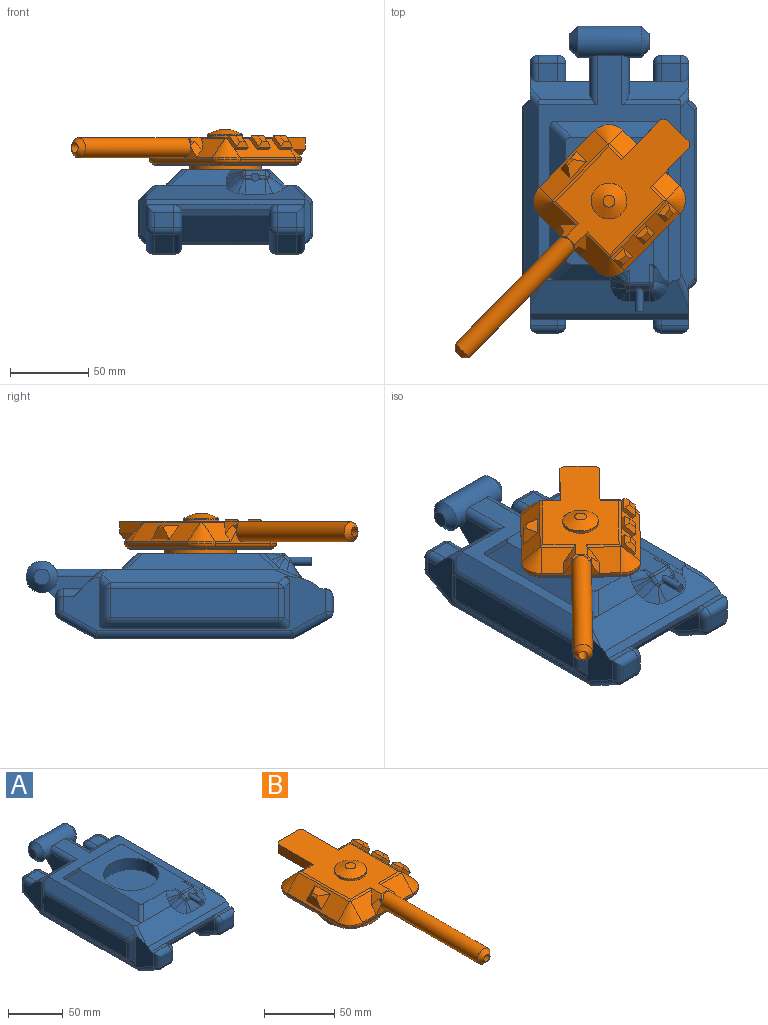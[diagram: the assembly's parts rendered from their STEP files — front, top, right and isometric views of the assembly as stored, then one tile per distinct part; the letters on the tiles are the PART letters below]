
ASSEMBLY  parts=2 mates=1
PART A: 179 faces, bbox 117.9x202.1x63.1 mm
  f0: plane 4.26x0.4mm, normal (0,-1,0), area 1.6mm2, adj f75,f86,f89,f96
  f1: plane 147.71x93.76mm, normal (0,0,1), area 3002mm2, adj f6,f44,f47,f48,f49,f51,f52,f54
  f2: plane 25.4x11.06mm, normal (0,0.71,-0.71), area 397.3mm2, adj f60,f61,f62,f63
  f3: plane 20.32x5.08mm, normal (0,1,0), area 83mm2, adj f4,f5,f60,f129
  f4: plane 55.88x20.32mm, normal (0,0.71,-0.71), area 1332.1mm2, adj f3,f9,f10,f23,f31,f60,f61,f62
  f5: plane 41.72x18.43mm, normal (0,0.71,0.71), area 577.8mm2, adj f3,f6,f13,f16,f60,f67,f74,f152
  f6: plane 39.72x5.32mm, normal (0,0.38,0.92), area 137.2mm2, adj f1,f5,f67,f74
  f7: plane 5.7x3.16mm, normal (0,-0.71,0.71), area 7.4mm2, adj f50,f51,f80,f99
  f8: plane 66.04x2.98mm, normal (0,-1,0), area 176.7mm2, adj f15,f46,f141,f165
  f9: plane 20.32x5.08mm, normal (0,1,0), area 83mm2, adj f4,f14,f61,f153
  f10: plane 109.66x55.88mm, normal (0,0,-1), area 6127.6mm2, adj f4,f23,f31,f45
  f11: plane 55.88x17.34mm, normal (0,-0.71,-0.71), area 1370.6mm2, adj f23,f31,f45,f46
  f12: plane 169.57x36.22mm, normal (-1,0,0), area 1238.2mm2, adj f14,f15,f30,f44,f48,f71,f73,f102
  f13: plane 169.57x36.22mm, normal (1,0,0), area 1238.2mm2, adj f5,f15,f18,f44,f47,f72,f74,f105
  f14: plane 41.72x18.43mm, normal (0,0.71,0.71), area 577.8mm2, adj f9,f12,f24,f49,f61,f66,f73,f176
  f15: plane 101.6x3.72mm, normal (0,-0.71,0.71), area 534.5mm2, adj f8,f12,f13,f18,f30,f44
  f16: plane 12.7x11.79mm, normal (0,0,1), area 149.7mm2, adj f5,f43,f129,f152
  f17: plane 12.7x9.7mm, normal (0,1,0), area 123.1mm2, adj f42,f43,f131,f150
  f18: plane 17.78x3.45mm, normal (0,0,1), area 61.4mm2, adj f13,f15,f38,f141
  f19: plane 12.7x9.7mm, normal (0,-1,0), area 123.1mm2, adj f38,f39,f139,f142
  f20: plane 21.63x12.7mm, normal (0,-0.48,-0.88), area 313.4mm2, adj f39,f40,f137,f144
  f21: plane 124.39x12.7mm, normal (0,0,-1), area 1579.8mm2, adj f40,f41,f135,f146
  f22: plane 21.63x12.7mm, normal (0,0.48,-0.88), area 313.4mm2, adj f41,f42,f133,f148
  f23: plane 167.64x21.59mm, normal (-1,0,0), area 680.5mm2, adj f4,f10,f11,f45,f46,f129,f131,f133
  f24: plane 12.7x11.79mm, normal (0,0,1), area 149.7mm2, adj f14,f37,f153,f176
  f25: plane 12.7x9.7mm, normal (0,1,0), area 123.1mm2, adj f36,f37,f155,f174
  f26: plane 21.63x12.7mm, normal (0,0.48,-0.88), area 313.4mm2, adj f35,f36,f157,f172
  f27: plane 124.39x12.7mm, normal (0,0,-1), area 1579.8mm2, adj f34,f35,f159,f170
  f28: plane 21.63x12.7mm, normal (0,-0.48,-0.88), area 313.4mm2, adj f33,f34,f161,f168
  f29: plane 12.7x9.7mm, normal (0,-1,0), area 123.1mm2, adj f32,f33,f163,f166
  f30: plane 17.78x3.45mm, normal (0,0,1), area 61.4mm2, adj f12,f15,f32,f165
  f31: plane 167.64x21.59mm, normal (1,0,0), area 680.5mm2, adj f4,f10,f11,f45,f46,f153,f155,f157
  f32: cylinder r=5.08mm len=17.78mm, axis (-1,0,0), area 121.6mm2, adj f29,f30,f164,f166
  f33: cylinder r=5.08mm len=12.7mm, axis (-1,0,0), area 68.9mm2, adj f28,f29,f162,f167
  f34: cylinder r=5.08mm len=12.7mm, axis (-1,0,0), area 32.4mm2, adj f27,f28,f160,f169
  f35: cylinder r=5.08mm len=12.7mm, axis (-1,0,0), area 32.4mm2, adj f26,f27,f158,f171
  f36: cylinder r=5.08mm len=12.7mm, axis (-1,0,0), area 68.9mm2, adj f25,f26,f156,f173
  f37: cylinder r=5.08mm len=12.7mm, axis (-1,0,0), area 101.3mm2, adj f24,f25,f154,f175
  f38: cylinder r=5.08mm len=17.78mm, axis (1,0,0), area 121.6mm2, adj f18,f19,f140,f142
  f39: cylinder r=5.08mm len=12.7mm, axis (1,0,0), area 68.9mm2, adj f19,f20,f138,f143
  f40: cylinder r=5.08mm len=12.7mm, axis (1,0,0), area 32.4mm2, adj f20,f21,f136,f145
  f41: cylinder r=5.08mm len=12.7mm, axis (1,0,0), area 32.4mm2, adj f21,f22,f134,f147
  f42: cylinder r=5.08mm len=12.7mm, axis (1,0,0), area 68.9mm2, adj f17,f22,f132,f149
  f43: cylinder r=5.08mm len=12.7mm, axis (1,0,0), area 101.3mm2, adj f16,f17,f130,f151
  f44: plane 101.62x21.7mm, normal (0,-0.38,0.92), area 1735.6mm2, adj f1,f12,f13,f15,f53,f71,f72,f93
  f45: plane 55.88x3.59mm, normal (0,-0.38,-0.92), area 217.3mm2, adj f10,f11,f23,f31
  f46: plane 56.81x3.61mm, normal (0,-0.92,-0.38), area 217.9mm2, adj f8,f11,f23,f31,f141,f165
  f47: plane 121.65x8.67mm, normal (0.71,0,0.71), area 1384.6mm2, adj f1,f13,f72,f74,f120,f122,f123
  f48: plane 121.65x8.67mm, normal (-0.71,0,0.71), area 1384.6mm2, adj f1,f12,f71,f73,f108,f113,f114
  f49: plane 39.72x5.32mm, normal (0,0.38,0.92), area 137.2mm2, adj f1,f14,f66,f73
  f50: plane 98.48x61.43mm, normal (0,0,1), area 2680.2mm2, adj f7,f51,f52,f53,f54,f55,f68,f69
  f51: plane 99.76x10.16mm, normal (0.71,0,0.71), area 1278.1mm2, adj f1,f7,f50,f68,f99
  f52: plane 69.02x10.16mm, normal (0,0.71,0.71), area 845.7mm2, adj f1,f50,f68,f69
  f53: plane 39.08x10.2mm, normal (0,-0.71,0.71), area 444.2mm2, adj f44,f50,f70,f90,f91,f92,f93
  f54: plane 94.42x10.16mm, normal (-0.71,0,0.71), area 1210.6mm2, adj f1,f50,f69,f70
  f55: cylinder r=25.4mm len=50.8mm, axis (0,0,1), area 2026.8mm2, adj f50,f56
  f56: plane 50.8x50.8mm, normal (0,0,1), area 2026.8mm2, adj f55
  f57: plane 4.26x0.4mm, normal (0,-1,0), area 1.6mm2, adj f75,f77,f78,f96
  f58: plane 12.25x3.44mm, normal (1,0,0), area 16mm2, adj f80,f81,f98,f99
  f59: plane 12.7x3.59mm, normal (0,-0.71,0.71), area 55.5mm2, adj f75,f78,f81,f84,f87,f89
  f60: plane 28.87x20.32mm, normal (1,0,0), area 389mm2, adj f2,f3,f4,f5,f62,f63,f67
  f61: plane 28.87x20.32mm, normal (-1,0,0), area 389mm2, adj f2,f4,f9,f14,f62,f63,f66
  f62: plane 25.4x17.81mm, normal (0,0,-1), area 452.5mm2, adj f2,f4,f60,f61
  f63: cylinder r=10.16mm len=40.64mm, axis (1,0,0), area 2190.3mm2, adj f1,f2,f60,f61,f66,f67,f177,f178
  f64: plane 10.16x10.16mm, normal (-1,0,0), area 81.1mm2, adj f178
  f65: plane 10.16x10.16mm, normal (1,0,0), area 81.1mm2, adj f177
  f66: cylinder r=5.08mm len=31.44mm, axis (0,-1,0), area 216.8mm2, adj f1,f14,f49,f61,f63
  f67: cylinder r=5.08mm len=31.44mm, axis (0,1,0), area 216.8mm2, adj f1,f5,f6,f60,f63
  f68: cylinder r=5.08mm len=13.75mm, axis (0.58,0.58,-0.58), area 93.6mm2, adj f1,f50,f51,f52
  f69: cylinder r=5.08mm len=13.75mm, axis (0.58,-0.58,0.58), area 93.6mm2, adj f1,f50,f52,f54
  f70: cylinder r=5.08mm len=13.75mm, axis (0.58,0.58,0.58), area 93.6mm2, adj f1,f50,f53,f54
  f71: cylinder r=5.08mm len=22.88mm, axis (0.36,0.86,0.36), area 77.2mm2, adj f1,f12,f44,f48
  f72: cylinder r=5.08mm len=22.88mm, axis (-0.36,0.86,0.36), area 77.2mm2, adj f1,f13,f44,f47
  f73: cylinder r=5.08mm len=13.59mm, axis (-0.58,0.58,-0.58), area 54mm2, adj f1,f12,f14,f48,f49,f113
  f74: cylinder r=5.08mm len=13.59mm, axis (0.58,0.58,-0.58), area 54mm2, adj f1,f5,f6,f13,f47,f120
  f75: cylinder r=2.54mm len=15.25mm, axis (0,1,0), area 214mm2, adj f0,f57,f59,f76,f78,f89,f96
  f76: plane 5.08x5.08mm, normal (0,-1,0), area 20.3mm2, adj f75
  f77: cylinder r=2.54mm len=0.97mm, axis (0,0,1), area 0.2mm2, adj f57,f79,f97
  f78: cylinder r=2.54mm len=4.04mm, axis (1,0,0), area 7.9mm2, adj f57,f59,f75,f79
  f79: sphere r=2.54mm, area 3.4mm2, adj f77,f78,f81,f98
  f80: cylinder r=2.54mm len=11.65mm, axis (0,1,0), area 42.8mm2, adj f7,f50,f58,f82,f99
  f81: cylinder r=2.54mm len=5.39mm, axis (0,0.71,0.71), area 19.5mm2, adj f58,f59,f79,f82,f98
  f82: sphere r=2.54mm, area 5.1mm2, adj f80,f81,f84
  f83: cylinder r=2.54mm len=7.44mm, axis (0,-1,0), area 14.1mm2, adj f50,f85,f90
  f84: cylinder r=2.54mm len=12.7mm, axis (1,0,0), area 25.3mm2, adj f50,f59,f82,f85
  f85: sphere r=2.54mm, area 4.8mm2, adj f83,f84,f87,f91
  f86: cylinder r=2.54mm len=0.97mm, axis (0,0,-1), area 0.2mm2, adj f0,f88,f95
  f87: cylinder r=2.54mm len=4.86mm, axis (0,0.71,0.71), area 16.1mm2, adj f59,f85,f88,f92,f93
  f88: sphere r=2.54mm, area 3.4mm2, adj f86,f87,f89,f94
  f89: cylinder r=2.54mm len=4.04mm, axis (1,0,0), area 7.9mm2, adj f0,f59,f75,f88
  f90: bspline ~14.62x11.56mm, area 85mm2, adj f50,f53,f83,f91
  f91: cone r=12.14mm half-angle=53.5deg, axis (0,0.71,-0.71), area 27.4mm2, adj f53,f85,f90,f92
  f92: plane 9.72x7.76mm, normal (-0.59,-0.57,0.57), area 29.9mm2, adj f53,f87,f91,f93
  f93: bspline ~10.05x9.93mm, area 56.4mm2, adj f44,f53,f87,f92,f94
  f94: cone r=11.88mm half-angle=55.4deg, axis (0,0.38,-0.92), area 81.9mm2, adj f44,f88,f93,f95
  f95: bspline ~9.78x6.46mm, area 34.2mm2, adj f44,f86,f94,f96
  f96: plane 12.7x9.39mm, normal (0,-0.83,0.56), area 139.5mm2, adj f0,f44,f57,f75,f95,f97
  f97: bspline ~10.21x7.05mm, area 34.2mm2, adj f44,f77,f96,f98
  f98: cone r=11.88mm half-angle=55.4deg, axis (0,0.38,-0.92), area 117.4mm2, adj f44,f58,f79,f81,f97,f99
  f99: bspline ~15.87x12.33mm, area 73.1mm2, adj f1,f7,f44,f51,f58,f80,f98
  f100: plane 107.55x18.65mm, normal (-1,0,0), area 2006mm2, adj f109,f114,f115,f119
  f101: plane 109.77x18.77mm, normal (1,0,0), area 2045mm2, adj f105,f120,f121,f123,f124,f128
  f102: plane 25.84x3.59mm, normal (-0.71,-0.71,0), area 113mm2, adj f12,f108,f109,f110
  f103: plane 114.74x3.59mm, normal (-0.71,0,-0.71), area 564.6mm2, adj f12,f110,f115,f116
  f104: plane 25.84x3.59mm, normal (-0.71,0.71,0), area 113mm2, adj f12,f113,f116,f119
  f105: plane 25.84x5.08mm, normal (0.71,0.71,0), area 149.1mm2, adj f13,f101,f120,f121
  f106: plane 114.74x3.59mm, normal (0.71,0,-0.71), area 564.6mm2, adj f13,f121,f124,f125
  f107: plane 25.84x3.59mm, normal (0.71,-0.71,0), area 113mm2, adj f13,f122,f125,f128
  f108: cylinder r=5.08mm len=7.18mm, axis (-0.58,0.58,-0.58), area 33.1mm2, adj f12,f48,f102,f111
  f109: cylinder r=5.08mm len=18.65mm, axis (0,0,-1), area 74.4mm2, adj f100,f102,f111,f112
  f110: cylinder r=5.08mm len=7.18mm, axis (0.58,-0.58,-0.58), area 33.1mm2, adj f12,f102,f103,f112
  f111: sphere r=5.08mm, area 7.6mm2, adj f108,f109,f114
  f112: sphere r=5.08mm, area 7.6mm2, adj f109,f110,f115
  f113: cylinder r=5.08mm len=8.98mm, axis (0.58,0.58,0.58), area 37.8mm2, adj f12,f48,f73,f104,f117
  f114: cylinder r=5.08mm len=107.55mm, axis (0,1,0), area 429.1mm2, adj f48,f100,f111,f117
  f115: cylinder r=5.08mm len=107.55mm, axis (0,-1,0), area 429.1mm2, adj f100,f103,f112,f118
  f116: cylinder r=5.08mm len=7.18mm, axis (-0.58,-0.58,0.58), area 33.1mm2, adj f12,f103,f104,f118
  f117: sphere r=5.08mm, area 7.6mm2, adj f113,f114,f119
  f118: sphere r=5.08mm, area 7.6mm2, adj f115,f116,f119
  f119: cylinder r=5.08mm len=18.65mm, axis (0,0,-1), area 74.4mm2, adj f100,f104,f117,f118
  f120: cylinder r=5.08mm len=10.47mm, axis (-0.58,0.58,0.58), area 44.5mm2, adj f13,f47,f74,f101,f105,f123
  f121: cylinder r=5.08mm len=9.23mm, axis (0.58,-0.58,0.58), area 43.2mm2, adj f13,f101,f105,f106,f124
  f122: cylinder r=5.08mm len=7.18mm, axis (0.58,0.58,-0.58), area 33.1mm2, adj f13,f47,f107,f126
  f123: cylinder r=5.08mm len=109.41mm, axis (0,1,0), area 432.8mm2, adj f47,f101,f120,f126
  f124: cylinder r=5.08mm len=109.41mm, axis (0,-1,0), area 432.8mm2, adj f101,f106,f121,f127
  f125: cylinder r=5.08mm len=7.18mm, axis (-0.58,-0.58,-0.58), area 33.1mm2, adj f13,f106,f107,f127
  f126: sphere r=5.08mm, area 8.8mm2, adj f122,f123,f128
  f127: sphere r=5.08mm, area 8.8mm2, adj f124,f125,f128
  f128: cylinder r=5.08mm len=18.65mm, axis (0,0,-1), area 74.4mm2, adj f101,f107,f126,f127
  f129: cylinder r=5.08mm len=11.79mm, axis (0,1,0), area 94.1mm2, adj f3,f16,f23,f130
  f130: sphere r=5.08mm, area 40.5mm2, adj f43,f129,f131
  f131: cylinder r=5.08mm len=9.7mm, axis (0,0,-1), area 77.4mm2, adj f17,f23,f130,f132
  f132: sphere r=5.08mm, area 27.6mm2, adj f42,f131,f133
  f133: cylinder r=5.08mm len=24.07mm, axis (0,-0.88,-0.48), area 196.9mm2, adj f22,f23,f132,f134
  f134: sphere r=5.08mm, area 13mm2, adj f41,f133,f135
  f135: cylinder r=5.08mm len=124.39mm, axis (0,-1,0), area 992.6mm2, adj f21,f23,f134,f136
  f136: sphere r=5.08mm, area 13mm2, adj f40,f135,f137
  f137: cylinder r=5.08mm len=24.07mm, axis (0,-0.88,0.48), area 196.9mm2, adj f20,f23,f136,f138
  f138: sphere r=5.08mm, area 27.6mm2, adj f39,f137,f139
  f139: cylinder r=5.08mm len=9.7mm, axis (0,0,1), area 77.4mm2, adj f19,f23,f138,f140
  f140: sphere r=5.08mm, area 40.5mm2, adj f38,f139,f141
  f141: cylinder r=5.08mm len=5.08mm, axis (0,1,0), area 28.5mm2, adj f8,f18,f23,f46,f140
  f142: cylinder r=5.08mm len=14.78mm, axis (0,0,-1), area 97.6mm2, adj f13,f19,f38,f143
  f143: sphere r=5.08mm, area 27.6mm2, adj f39,f142,f144
  f144: cylinder r=5.08mm len=24.07mm, axis (0,0.88,-0.48), area 196.9mm2, adj f13,f20,f143,f145
  f145: sphere r=5.08mm, area 13mm2, adj f40,f144,f146
  f146: cylinder r=5.08mm len=124.39mm, axis (0,1,0), area 992.6mm2, adj f13,f21,f145,f147
  f147: sphere r=5.08mm, area 13mm2, adj f41,f146,f148
  f148: cylinder r=5.08mm len=24.07mm, axis (0,0.88,0.48), area 196.9mm2, adj f13,f22,f147,f149
  f149: sphere r=5.08mm, area 27.6mm2, adj f42,f148,f150
  f150: cylinder r=5.08mm len=9.7mm, axis (0,0,1), area 77.4mm2, adj f13,f17,f149,f151
  f151: sphere r=5.08mm, area 40.5mm2, adj f43,f150,f152
  f152: cylinder r=5.08mm len=11.79mm, axis (0,-1,0), area 73.8mm2, adj f5,f13,f16,f151
  f153: cylinder r=5.08mm len=11.79mm, axis (0,-1,0), area 94.1mm2, adj f9,f24,f31,f154
  f154: sphere r=5.08mm, area 40.5mm2, adj f37,f153,f155
  f155: cylinder r=5.08mm len=9.7mm, axis (0,0,1), area 77.4mm2, adj f25,f31,f154,f156
  f156: sphere r=5.08mm, area 27.6mm2, adj f36,f155,f157
  f157: cylinder r=5.08mm len=24.07mm, axis (0,0.88,0.48), area 196.9mm2, adj f26,f31,f156,f158
  f158: sphere r=5.08mm, area 13mm2, adj f35,f157,f159
  f159: cylinder r=5.08mm len=124.39mm, axis (0,1,0), area 992.6mm2, adj f27,f31,f158,f160
  f160: sphere r=5.08mm, area 13mm2, adj f34,f159,f161
  f161: cylinder r=5.08mm len=24.07mm, axis (0,0.88,-0.48), area 196.9mm2, adj f28,f31,f160,f162
  f162: sphere r=5.08mm, area 27.6mm2, adj f33,f161,f163
  f163: cylinder r=5.08mm len=9.7mm, axis (0,0,-1), area 77.4mm2, adj f29,f31,f162,f164
  f164: sphere r=5.08mm, area 40.5mm2, adj f32,f163,f165
  f165: cylinder r=5.08mm len=5.08mm, axis (0,-1,0), area 28.5mm2, adj f8,f30,f31,f46,f164
  f166: cylinder r=5.08mm len=14.78mm, axis (0,0,-1), area 97.6mm2, adj f12,f29,f32,f167
  f167: sphere r=5.08mm, area 27.6mm2, adj f33,f166,f168
  f168: cylinder r=5.08mm len=24.07mm, axis (0,0.88,-0.48), area 196.9mm2, adj f12,f28,f167,f169
  f169: sphere r=5.08mm, area 13mm2, adj f34,f168,f170
  f170: cylinder r=5.08mm len=124.39mm, axis (0,1,0), area 992.6mm2, adj f12,f27,f169,f171
  f171: sphere r=5.08mm, area 13mm2, adj f35,f170,f172
  f172: cylinder r=5.08mm len=24.07mm, axis (0,0.88,0.48), area 196.9mm2, adj f12,f26,f171,f173
  f173: sphere r=5.08mm, area 32.3mm2, adj f36,f172,f174
  f174: cylinder r=5.08mm len=9.7mm, axis (0,0,1), area 77.4mm2, adj f12,f25,f173,f175
  f175: sphere r=5.08mm, area 40.5mm2, adj f37,f174,f176
  f176: cylinder r=5.08mm len=11.79mm, axis (0,-1,0), area 73.8mm2, adj f12,f14,f24,f175
  f177: cone r=5.08mm half-angle=45deg, axis (-1,0,0), area 344mm2, adj f63,f65
  f178: cone r=5.08mm half-angle=45deg, axis (1,0,0), area 344mm2, adj f63,f64
PART B: 111 faces, bbox 78.3x200.4x38.1 mm
  f0: plane 17.78x11.96mm, normal (0,0.71,0.71), area 233mm2, adj f2,f7,f20,f44,f47
  f1: plane 17.78x11.96mm, normal (0,0.71,0.71), area 233mm2, adj f3,f23,f39,f46,f50
  f2: plane 19.27x1.49mm, normal (0,1,0), area 27.6mm2, adj f0,f4,f14,f47
  f3: plane 19.27x1.49mm, normal (0,1,0), area 27.6mm2, adj f1,f4,f15,f50
  f4: cylinder r=2.54mm len=50.8mm, axis (-1,0,0), area 89.2mm2, adj f2,f3,f31,f47,f50,f61,f62,f106
  f5: plane 50.8x11.96mm, normal (0.71,0,0.71), area 549.3mm2, adj f13,f20,f21,f37,f79,f82,f84,f86
  f6: plane 50.8x11.96mm, normal (-0.71,0,0.71), area 664.2mm2, adj f16,f23,f24,f41,f75,f76,f77,f78
  f7: plane 13.14x1.8mm, normal (0,0.38,0.92), area 24.3mm2, adj f0,f18,f20,f37,f44
  f8: plane 50.8x11.65mm, normal (0,-1,0), area 129.9mm2, adj f9,f12,f17,f22,f25,f26,f27,f40
  f9: plane 20.85x11.96mm, normal (0,-0.71,0.71), area 269.6mm2, adj f8,f21,f36,f38,f108
  f10: cylinder r=22.86mm len=45.72mm, axis (0,0,-1), area 2189mm2, adj f11,f19
  f11: plane 45.72x45.72mm, normal (0,0,-1), area 1641.7mm2, adj f10
  f12: cylinder r=12.7mm len=12.7mm, axis (0,0,-1), area 29.7mm2, adj f8,f13,f21,f57
  f13: plane 50.8x1.49mm, normal (1,0,0), area 75.6mm2, adj f5,f12,f14,f59
  f14: cylinder r=12.7mm len=12.7mm, axis (0,0,-1), area 29.7mm2, adj f2,f13,f20,f61
  f15: cylinder r=12.7mm len=12.7mm, axis (0,0,-1), area 29.7mm2, adj f3,f16,f23,f62
  f16: plane 50.8x1.49mm, normal (-1,0,0), area 75.6mm2, adj f6,f15,f17,f60
  f17: cylinder r=12.7mm len=12.7mm, axis (0,0,-1), area 29.7mm2, adj f8,f16,f24,f58
  f18: plane 98.01x48.7mm, normal (0,0,1), area 3007.6mm2, adj f7,f36,f37,f38,f39,f40,f41,f42
  f19: plane 69.02x69.02mm, normal (0,0,-1), area 3050.2mm2, adj f10,f63,f64,f65,f66,f67,f68,f69
  f20: cone r=12.7mm half-angle=45deg, axis (0,0,-1), area 178.6mm2, adj f0,f5,f7,f14,f37,f92
  f21: cone r=12.7mm half-angle=45deg, axis (0,0,-1), area 178.6mm2, adj f5,f9,f12,f36,f37,f81
  f22: plane 20.85x11.96mm, normal (0,-0.71,0.71), area 269.6mm2, adj f8,f24,f42,f43,f107
  f23: cone r=12.7mm half-angle=45deg, axis (0,0,-1), area 178.6mm2, adj f1,f6,f15,f39,f41
  f24: cone r=12.7mm half-angle=45deg, axis (0,0,-1), area 178.6mm2, adj f6,f17,f22,f41,f43
  f25: plane 2.98x2.98mm, normal (1,0,0), area 4.4mm2, adj f8,f38,f108
  f26: plane 2.98x2.98mm, normal (-1,0,0), area 4.4mm2, adj f8,f42,f107
  f27: cylinder r=6.35mm len=98.81mm, axis (0,1,0), area 3867.7mm2, adj f8,f40,f109
  f28: plane 50.8x1.05mm, normal (0.71,0,-0.71), area 75.6mm2, adj f29,f30,f59,f67
  f29: cone r=12.7mm half-angle=45deg, axis (0,0,1), area 26.7mm2, adj f28,f31,f61,f69
  f30: cone r=12.7mm half-angle=45deg, axis (0,0,1), area 26.7mm2, adj f28,f32,f57,f65
  f31: plane 50.8x1.05mm, normal (0,0.71,-0.71), area 75.6mm2, adj f4,f29,f33,f70
  f32: plane 50.8x1.05mm, normal (0,-0.71,-0.71), area 75.6mm2, adj f30,f34,f56,f63
  f33: cone r=12.7mm half-angle=45deg, axis (0,0,1), area 26.7mm2, adj f31,f35,f62,f68
  f34: cone r=12.7mm half-angle=45deg, axis (0,0,1), area 26.7mm2, adj f32,f35,f58,f64
  f35: plane 50.8x1.05mm, normal (-0.71,0,-0.71), area 75.6mm2, adj f33,f34,f60,f66
  f36: plane 22.03x1.8mm, normal (0,-0.38,0.92), area 40.9mm2, adj f9,f18,f21,f37,f38
  f37: plane 51.67x1.8mm, normal (0.38,0,0.92), area 98mm2, adj f5,f7,f18,f20,f21,f36,f80,f85
  f38: plane 13.75x7.62mm, normal (0.71,0,0.71), area 62.9mm2, adj f9,f18,f25,f36,f40,f108
  f39: plane 13.14x1.8mm, normal (0,0.38,0.92), area 24.3mm2, adj f1,f18,f23,f41,f46
  f40: plane 12.7x2.54mm, normal (0,-0.71,0.71), area 14.6mm2, adj f8,f18,f27,f38,f42
  f41: plane 51.67x1.8mm, normal (-0.38,0,0.92), area 98mm2, adj f6,f18,f23,f24,f39,f43
  f42: plane 13.75x7.62mm, normal (-0.71,0,0.71), area 62.9mm2, adj f18,f22,f26,f40,f43,f107
  f43: plane 22.03x1.8mm, normal (0,-0.38,0.92), area 40.9mm2, adj f18,f22,f24,f41,f42
  f44: plane 35.56x7.62mm, normal (1,0,0), area 234.3mm2, adj f0,f7,f18,f47,f48
  f45: plane 20.32x7.62mm, normal (0,1,0), area 154.8mm2, adj f18,f48,f51,f53
  f46: plane 35.56x7.62mm, normal (-1,0,0), area 234.3mm2, adj f1,f18,f39,f50,f53
  f47: plane 26.89x7.62mm, normal (0.71,0,-0.71), area 235.1mm2, adj f0,f2,f4,f44,f49,f51,f106
  f48: plane 7.62x2.54mm, normal (0.71,0.71,0), area 27.4mm2, adj f18,f44,f45,f49
  f49: plane 2.54x2.54mm, normal (0.58,0.58,-0.58), area 5.6mm2, adj f47,f48,f51
  f50: plane 26.89x7.62mm, normal (-0.71,0,-0.71), area 235.1mm2, adj f1,f3,f4,f46,f51,f52,f106
  f51: plane 20.32x7.62mm, normal (0,0.71,-0.71), area 182.5mm2, adj f45,f47,f49,f50,f52,f106
  f52: plane 2.54x2.54mm, normal (-0.58,0.58,-0.58), area 5.6mm2, adj f50,f51,f53
  f53: plane 7.62x2.54mm, normal (-0.71,0.71,0), area 27.4mm2, adj f18,f45,f46,f52
  f54: cylinder r=11.43mm len=22.86mm, axis (0,0,-1), area 106.9mm2, adj f18,f71
  f55: plane 7.62x7.62mm, normal (0,0,1), area 45.6mm2, adj f110
  f56: cylinder r=2.54mm len=50.8mm, axis (1,0,0), area 101.3mm2, adj f8,f32,f57,f58
  f57: torus R=10.16mm, axis (0,0,-1), area 39mm2, adj f12,f30,f56,f59
  f58: torus R=10.16mm, axis (0,0,-1), area 39mm2, adj f17,f34,f56,f60
  f59: cylinder r=2.54mm len=50.8mm, axis (0,1,0), area 101.3mm2, adj f13,f28,f57,f61
  f60: cylinder r=2.54mm len=50.8mm, axis (0,-1,0), area 101.3mm2, adj f16,f35,f58,f62
  f61: torus R=10.16mm, axis (0,0,-1), area 39mm2, adj f4,f14,f29,f59
  f62: torus R=10.16mm, axis (0,0,-1), area 39mm2, adj f4,f15,f33,f60
  f63: cylinder r=2.54mm len=50.8mm, axis (1,0,0), area 101.3mm2, adj f19,f32,f64,f65
  f64: torus R=9.11mm, axis (0,0,1), area 31.5mm2, adj f19,f34,f63,f66
  f65: torus R=9.11mm, axis (0,0,1), area 31.5mm2, adj f19,f30,f63,f67
  f66: cylinder r=2.54mm len=50.8mm, axis (0,1,0), area 101.3mm2, adj f19,f35,f64,f68
  f67: cylinder r=2.54mm len=50.8mm, axis (0,1,0), area 101.3mm2, adj f19,f28,f65,f69
  f68: torus R=9.11mm, axis (0,0,1), area 31.5mm2, adj f19,f33,f66,f70
  f69: torus R=9.11mm, axis (0,0,1), area 31.5mm2, adj f19,f29,f67,f70
  f70: cylinder r=2.54mm len=50.8mm, axis (1,0,0), area 101.3mm2, adj f19,f31,f68,f69
  f71: torus R=8.89mm, axis (0,0,1), area 32.6mm2, adj f54,f110
  f72: cylinder r=3.05mm len=23.62mm, axis (0,-1,0), area 452.4mm2, adj f73,f109
  f73: plane 6.1x6.1mm, normal (0,-1,0), area 29.2mm2, adj f72
  f74: plane 5.17x1.8mm, normal (-0.71,0,0.71), area 13.1mm2, adj f75,f76,f77,f78
  f75: plane 15.33x7.18mm, normal (0,0,1), area 73.6mm2, adj f6,f74,f76,f77
  f76: plane 8.98x8.98mm, normal (-0.5,0.71,0.5), area 54.7mm2, adj f6,f74,f75,f78
  f77: plane 8.98x8.98mm, normal (-0.5,-0.71,0.5), area 54.7mm2, adj f6,f74,f75,f78
  f78: plane 15.33x7.18mm, normal (-1,0,0), area 73.6mm2, adj f6,f74,f76,f77
  f79: plane 8.98x8.98mm, normal (0,1,0), area 25.8mm2, adj f5,f80,f82,f102
  f80: plane 10.16x1.8mm, normal (-0.71,0,0.71), area 25.8mm2, adj f37,f79,f81,f104
  f81: plane 8.98x8.98mm, normal (0,-1,0), area 25.8mm2, adj f21,f80,f82,f105
  f82: plane 10.16x1.8mm, normal (0.71,0,-0.71), area 25.8mm2, adj f5,f79,f81,f103
  f83: plane 5.08x3.59mm, normal (0.71,0,0.71), area 25.8mm2, adj f102,f103,f104,f105
  f84: plane 8.98x8.98mm, normal (0,1,0), area 25.8mm2, adj f5,f85,f87,f100
  f85: plane 10.16x1.8mm, normal (-0.71,0,0.71), area 25.8mm2, adj f37,f84,f86,f98
  f86: plane 8.98x8.98mm, normal (0,-1,0), area 25.8mm2, adj f5,f85,f87,f99
  f87: plane 10.16x1.8mm, normal (0.71,0,-0.71), area 25.8mm2, adj f5,f84,f86,f101
  f88: plane 5.08x3.59mm, normal (0.71,0,0.71), area 25.8mm2, adj f98,f99,f100,f101
  f89: plane 10.16x1.8mm, normal (-0.71,0,0.71), area 25.8mm2, adj f37,f90,f92,f94
  f90: plane 8.98x8.98mm, normal (0,-1,0), area 25.8mm2, adj f5,f89,f91,f95
  f91: plane 10.16x1.8mm, normal (0.71,0,-0.71), area 25.8mm2, adj f5,f90,f92,f97
  f92: plane 8.98x8.98mm, normal (0,1,0), area 25.8mm2, adj f20,f89,f91,f96
  f93: plane 5.08x3.59mm, normal (0.71,0,0.71), area 25.8mm2, adj f94,f95,f96,f97
  f94: plane 10.16x3.59mm, normal (0,0,1), area 27.4mm2, adj f89,f93,f95,f96
  f95: plane 7.18x7.18mm, normal (0.5,-0.71,0.5), area 27.4mm2, adj f90,f93,f94,f97
  f96: plane 7.18x7.18mm, normal (0.5,0.71,0.5), area 27.4mm2, adj f92,f93,f94,f97
  f97: plane 10.16x3.59mm, normal (1,0,0), area 27.4mm2, adj f91,f93,f95,f96
  f98: plane 10.16x3.59mm, normal (0,0,1), area 27.4mm2, adj f85,f88,f99,f100
  f99: plane 7.18x7.18mm, normal (0.5,-0.71,0.5), area 27.4mm2, adj f86,f88,f98,f101
  f100: plane 7.18x7.18mm, normal (0.5,0.71,0.5), area 27.4mm2, adj f84,f88,f98,f101
  f101: plane 10.16x3.59mm, normal (1,0,0), area 27.4mm2, adj f87,f88,f99,f100
  f102: plane 7.18x7.18mm, normal (0.5,0.71,0.5), area 27.4mm2, adj f79,f83,f103,f104
  f103: plane 10.16x3.59mm, normal (1,0,0), area 27.4mm2, adj f82,f83,f102,f105
  f104: plane 10.16x3.59mm, normal (0,0,1), area 27.4mm2, adj f80,f83,f102,f105
  f105: plane 7.18x7.18mm, normal (0.5,-0.71,0.5), area 27.4mm2, adj f81,f83,f103,f104
  f106: plane 16.96x10.16mm, normal (0,0,-1), area 172.3mm2, adj f4,f47,f50,f51
  f107: plane 10.16x5.08mm, normal (-0.71,-0.5,0.5), area 40.9mm2, adj f8,f22,f26,f42
  f108: plane 10.16x5.08mm, normal (0.71,-0.5,0.5), area 40.9mm2, adj f8,f9,f25,f38
  f109: cone r=1.27mm half-angle=45deg, axis (0,1,0), area 137.9mm2, adj f27,f72
  f110: cone r=3.81mm half-angle=67.5deg, axis (0,0,-1), area 391.7mm2, adj f55,f71
PLACE A t=(10.27,-14.24,-11.87)mm fixed
PLACE B rot(axis=(0,0,-1),44.4deg) t=(-81.14,85.96,4.64)mm
MATE revolute B.f10 <-> A.f55  axis (0,0,-1) through (10.27,-14.24,4.64)mm
